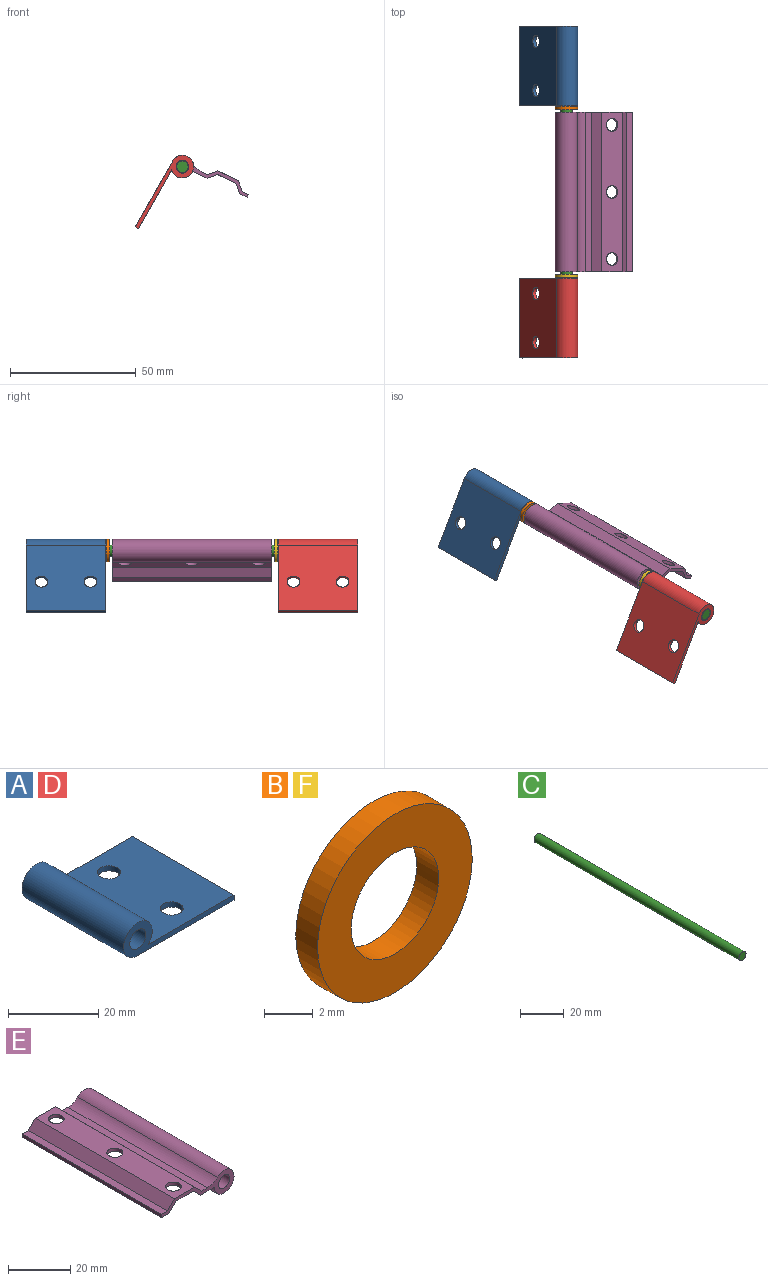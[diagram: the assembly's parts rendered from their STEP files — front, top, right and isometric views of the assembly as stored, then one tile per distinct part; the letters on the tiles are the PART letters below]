
ASSEMBLY  parts=6 mates=9
PART A: 9 faces, bbox 34.5x31.8x9 mm
  f0: plane 31.75x26.81mm, normal (0,0,1), area 810.7mm2, adj f1,f4,f5,f6,f7,f8
  f1: cylinder r=4.48mm len=31.75mm, axis (0,1,0), area 778.8mm2, adj f0,f2,f5,f6
  f2: plane 31.75x30.06mm, normal (0,0,-1), area 913.9mm2, adj f1,f4,f5,f6,f7,f8
  f3: cylinder r=2.54mm len=31.75mm, axis (0,1,0), area 506.7mm2, adj f5,f6
  f4: plane 31.75x1.4mm, normal (1,0,0), area 44.4mm2, adj f0,f2,f5,f6
  f5: plane 34.54x8.97mm, normal (0,-1,0), area 81.7mm2, adj f0,f1,f2,f3,f4
  f6: plane 34.54x8.97mm, normal (0,1,0), area 81.7mm2, adj f0,f1,f2,f3,f4
  f7: cylinder r=2.54mm len=5.08mm, axis (0,0,1), area 22.3mm2, adj f0,f2
  f8: cylinder r=2.54mm len=5.08mm, axis (0,0,1), area 22.3mm2, adj f0,f2
PART B: 4 faces, bbox 9x1.3x9 mm
  f0: cylinder r=2.54mm len=5.08mm, axis (0,-1,0), area 20.3mm2, adj f2,f3
  f1: cylinder r=4.48mm len=8.97mm, axis (0,-1,0), area 35.8mm2, adj f2,f3
  f2: plane 8.97x8.97mm, normal (0,1,0), area 42.9mm2, adj f0,f1
  f3: plane 8.97x8.97mm, normal (0,-1,0), area 42.9mm2, adj f0,f1
PART C: 3 faces, bbox 4.6x132.1x4.6 mm
  f0: cylinder r=2.29mm len=132.08mm, axis (0,1,0), area 1897.1mm2, adj f1,f2
  f1: plane 4.57x4.57mm, normal (0,-1,0), area 16.4mm2, adj f0
  f2: plane 4.57x4.57mm, normal (0,1,0), area 16.4mm2, adj f0
PART D: same geometry as A
PART E: 19 faces, bbox 33x63.5x9 mm
  f0: plane 63.5x3.21mm, normal (0.71,0,-0.71), area 288.5mm2, adj f1,f12,f14,f15
  f1: plane 63.5x7.98mm, normal (0,0,-1), area 445.6mm2, adj f0,f2,f14,f15,f16,f17,f18
  f2: plane 63.5x3.21mm, normal (-0.71,0,-0.71), area 288.5mm2, adj f1,f3,f14,f15
  f3: plane 63.5x6.35mm, normal (0,0,-1), area 403.2mm2, adj f2,f4,f14,f15
  f4: cylinder r=4.48mm len=63.5mm, axis (0,1,0), area 1563.8mm2, adj f3,f5,f14,f15
  f5: cylinder r=6.35mm len=63.5mm, axis (0,1,0), area 314.8mm2, adj f4,f6,f14,f15
  f6: plane 63.5x2.65mm, normal (0,0,1), area 168.4mm2, adj f5,f7,f14,f15
  f7: plane 63.5x3.14mm, normal (0.71,0,0.71), area 281.7mm2, adj f6,f8,f14,f15
  f8: plane 63.5x9.14mm, normal (0,0,1), area 519.3mm2, adj f7,f9,f14,f15,f16,f17,f18
  f9: plane 63.5x3.21mm, normal (-0.71,0,0.71), area 288.5mm2, adj f8,f10,f14,f15
  f10: plane 63.5x2.78mm, normal (0,0,1), area 176.3mm2, adj f9,f11,f14,f15
  f11: plane 63.5x1.27mm, normal (-1,0,0), area 80.6mm2, adj f10,f12,f14,f15
  f12: plane 63.5x3.3mm, normal (0,0,-1), area 209.7mm2, adj f0,f11,f14,f15
  f13: cylinder r=2.54mm len=63.5mm, axis (0,1,0), area 1013.4mm2, adj f14,f15
  f14: plane 33.02x8.97mm, normal (0,-1,0), area 79mm2, adj f0,f1,f2,f3,f4,f5,f6,f7
  f15: plane 33.02x8.97mm, normal (0,1,0), area 79mm2, adj f0,f1,f2,f3,f4,f5,f6,f7
  f16: cylinder r=2.54mm len=5.08mm, axis (0,0,-1), area 20.3mm2, adj f1,f8
  f17: cylinder r=2.54mm len=5.08mm, axis (0,0,-1), area 20.3mm2, adj f1,f8
  f18: cylinder r=2.54mm len=5.08mm, axis (0,0,-1), area 20.3mm2, adj f1,f8
PART F: same geometry as B
PLACE A rot(axis=(0,1,0),119.5deg) t=(-9.14,0,8.45)mm
PLACE B rot(axis=(0,1,0),5.6deg) t=(-9.14,-33.53,8.45)mm
PLACE C t=(-9.14,31.75,8.45)mm fixed
PLACE D rot(axis=(0,1,0),119.5deg) t=(-9.14,-100.33,8.45)mm
PLACE E rot(axis=(-0.22,0,-0.98),180deg) t=(-9.14,-261.62,8.45)mm
PLACE F rot(axis=(0,1,0),5.6deg) t=(-9.14,-100.33,8.45)mm
MATE parallel A.f0 <-> D.f0  axis (0.87,0,-0.49) through (-20.03,-15.88,-4.52)mm
MATE planar A.f3 <-> C.f0  axis (0,1,0) through (-9.14,0,8.45)mm
MATE cylindrical C.f0 <-> A.f3  axis (0,1,0) through (-9.14,0,8.45)mm
MATE cylindrical B.f0 <-> C.f0  axis (0,-1,0) through (-9.14,-33.27,8.45)mm
MATE planar B.f1 <-> A.f3  axis (0,1,0) through (-9.14,-32,8.45)mm
MATE cylindrical F.f1 <-> C.f0  axis (0,-1,0) through (-9.14,-100.08,8.45)mm
MATE revolute D.f3 <-> C.f0  axis (0,-1,0) through (-9.14,-132.08,8.45)mm
MATE revolute E.f4 <-> C.f0  axis (0,-1,0) through (-9.14,-66.04,8.45)mm
MATE planar F.f1 <-> D.f3  axis (0,-1,0) through (-9.14,-100.08,8.45)mm
